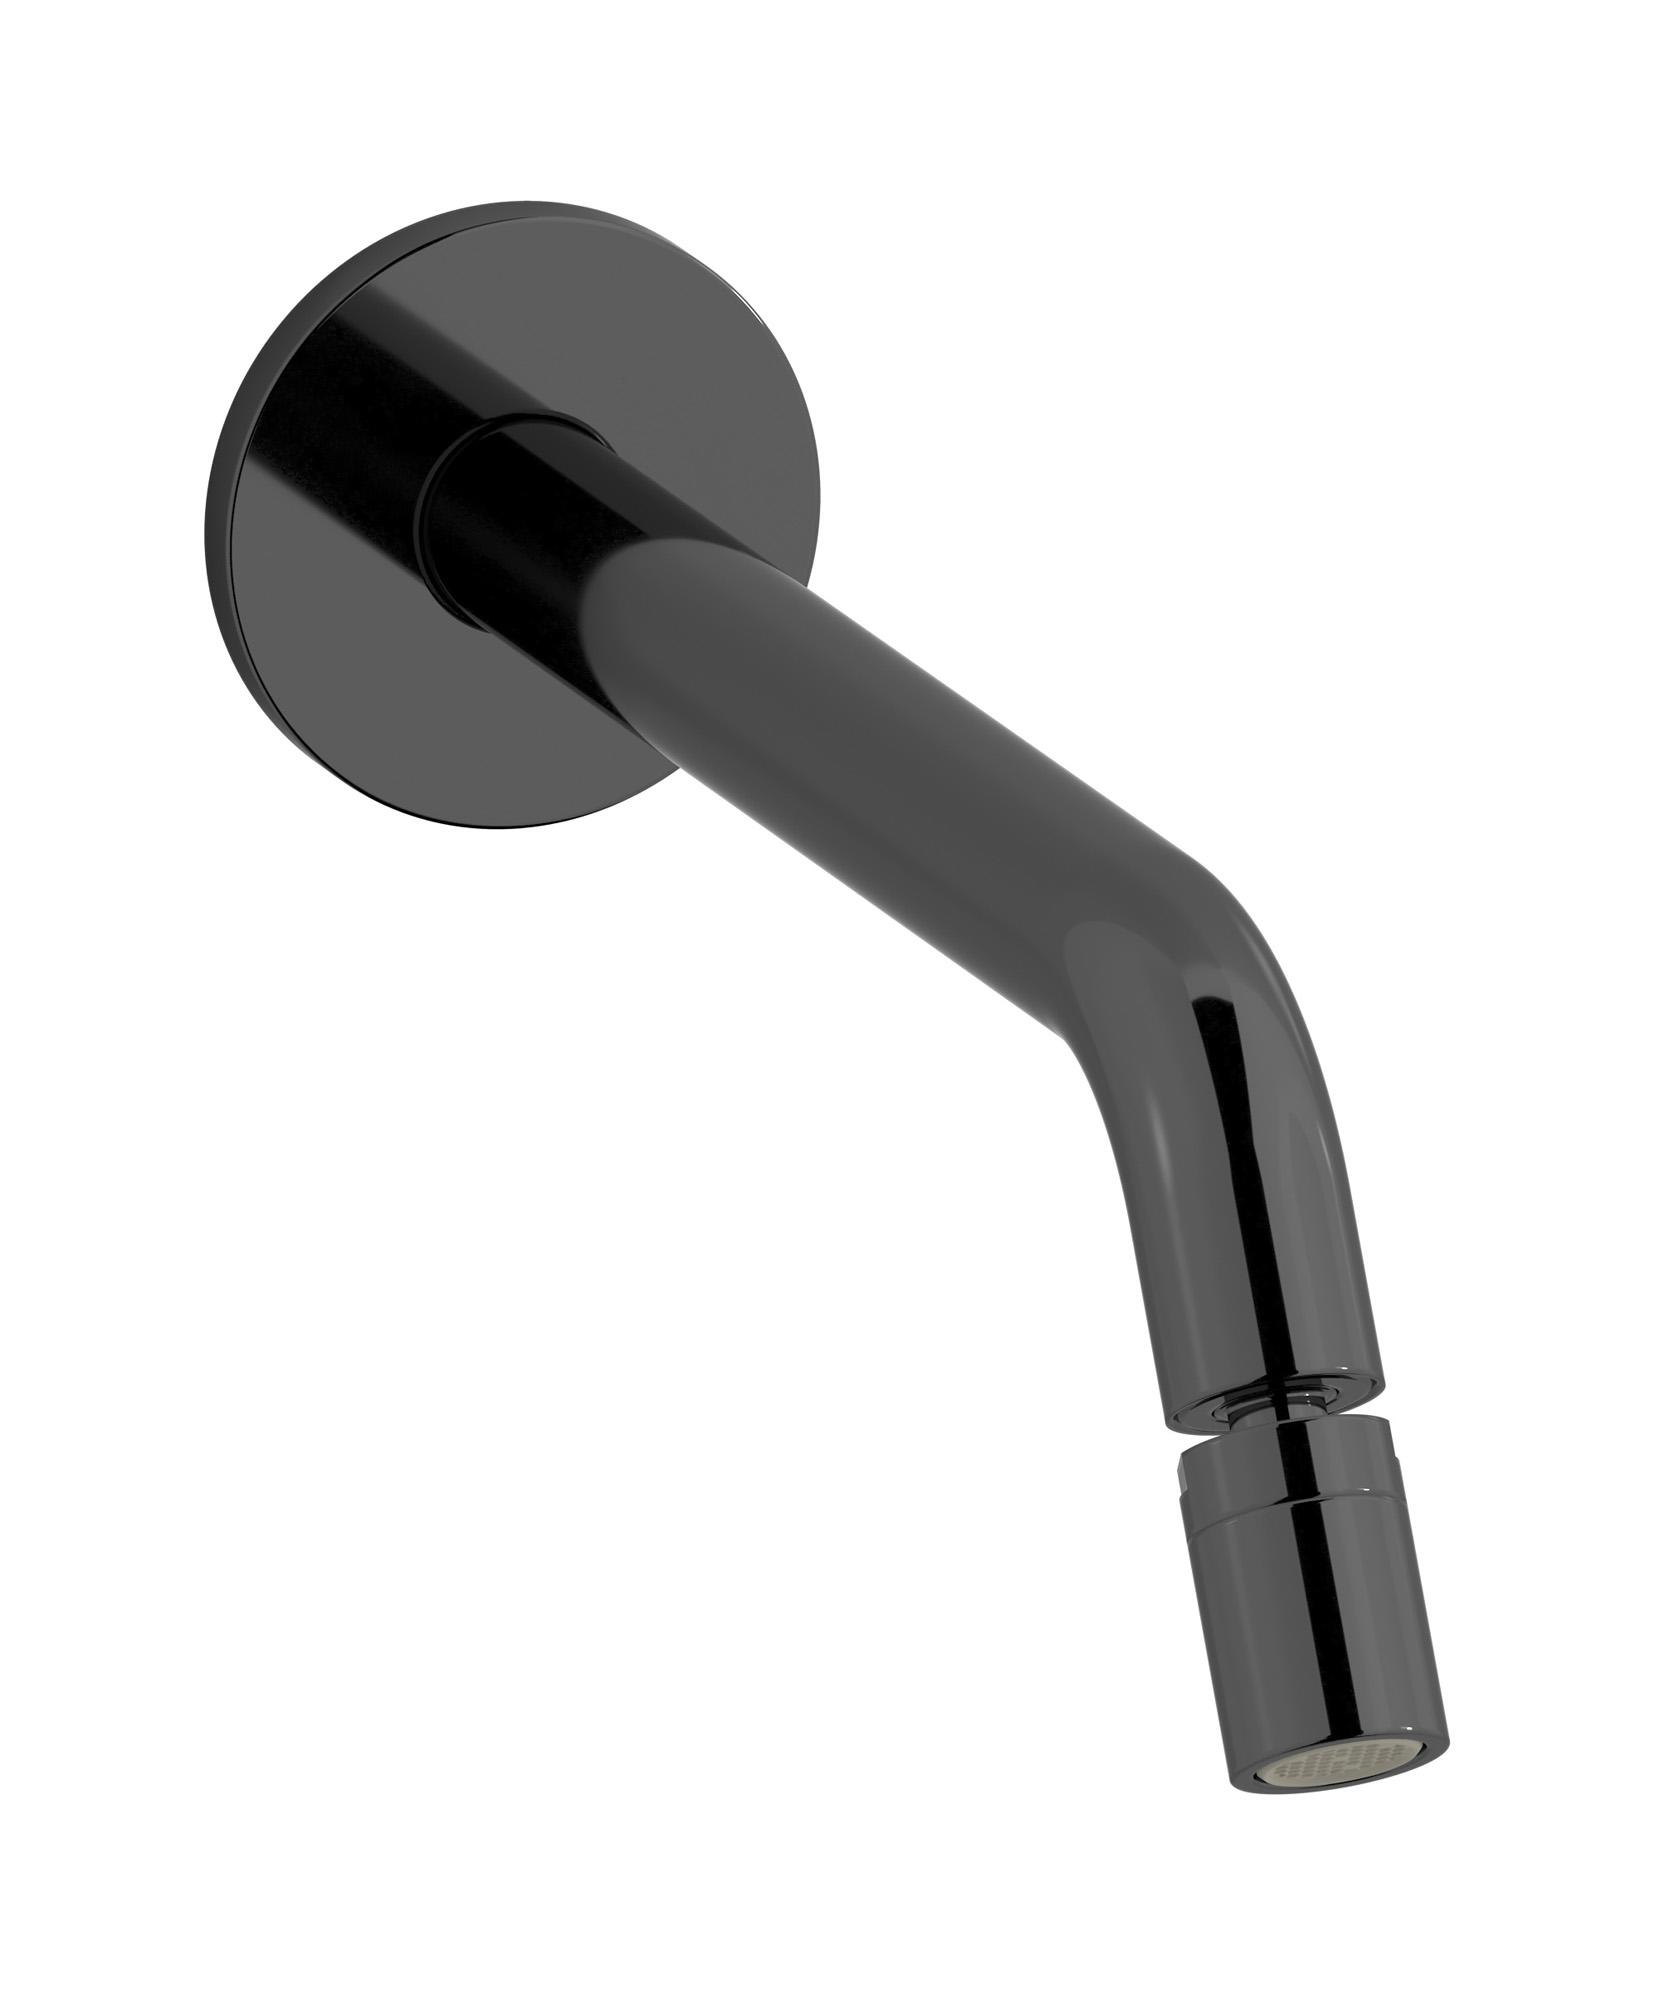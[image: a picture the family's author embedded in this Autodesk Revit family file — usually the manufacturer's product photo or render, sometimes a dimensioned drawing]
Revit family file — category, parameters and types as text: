
# Revit family: RX317
name_source: partatom
category: Apparecchi idraulici
units: mm (PartAtom-declared; Revit-internal decimal feet)

## family parameters
Basato su piano di lavoro = No
Condiviso = No
Mantieni orientamento annotazione = No
Numero OmniClass = 23.45.55.17
Punto di calcolo locali = No
Quota connettore circolare = Usa diametro
Sempre verticale = Sì
Taglio con vuoti quando caricato = No
Tipo di parte = Normale
Titolo OmniClass = Mixing Faucets

## types (12) — shared parameters
Commenti sul tipo = Bidet wall mounted spout complete with drain
Connessione CW = No
Connessione HW = No
Connessione di scarico = No
Connessione di ventilazione = No
Descrizione = Bidet wall mounted spout complete with drain
Produttore = IB Rubinetterie S.p.A.
URL = https://www.weareib.it
Water inlet = 10 mm  [stored 0.0328084 ft]
zero-valued in all types: Prospetto di default

## per-type parameters (varying)
| type | Finishes surface | Immagine tipo | Modello |
| Chrome | IB_Chrome | RX317CC.jpg | RX317CC |
| Black Chrome | IB_Black chrome | RX317CF.jpg | RX317CF |
| Brushed Black Chrome | IB_Brushed black chrome | RX317CS.jpg | RX317CS |
| Pale Gold | IB_Pale gold | RX317II.jpg | RX317II |
| Brushed Pale Gold | IB_brushed pale gold | RX317IS.jpg | RX317IS |
| Matt Black | IB_matt black | RX317NP.jpg | RX317NP |
| Natural Brass | IB_Brass | RX317ON.jpg | RX317ON |
| Gold | IB_gold | RX317OO.jpg | RX317OO |
| Brushed Gold | IB_brushed gold | RX317OS.jpg | RX317OS |
| Rose Gold | IB_Rose gold | RX317RS.jpg | RX317RS |
| Brushed Rose Gold | IB_Brushed rose gold | RX317SR.jpg | RX317SR |
| Brushed Nickel | IB_Brushed nickel | RX317SS.jpg | RX317SS |

note: [stored X ft] marks values corroborated as IEEE doubles in the binary element streams (Revit-internal decimal feet)
